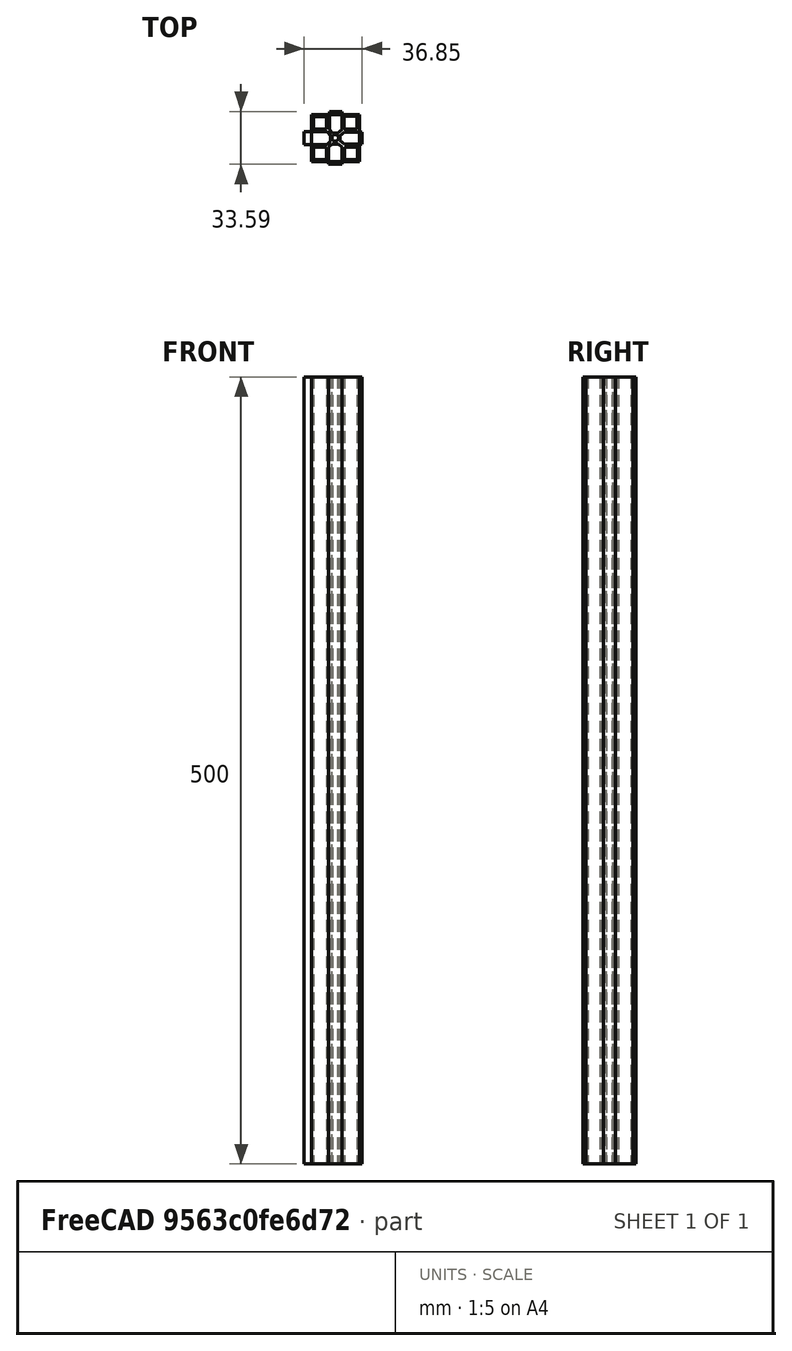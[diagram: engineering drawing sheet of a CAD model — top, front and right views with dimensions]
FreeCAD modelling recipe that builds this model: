
FCSTD DOCUMENT  (FreeCAD 0.16R6712 (Git))
Label: Perfil - Gslot
License: All rights reserved
LicenseURL: http://en.wikipedia.org/wiki/All_rights_reserved
objects: Sketcher::SketchObject×2, PartDesign::Pad×1, PartDesign::Pocket×1
note: 6 computed .brp shape members not serialized (recipe doc carries the construction recipe); baked Part::Feature solids carry a one-line shape summary decoded from their .brp

FEATURE [Sketcher::SketchObject] Sketch
  sketch-geometry (4):
    g0: LineSegment StartX=0 StartY=0 StartZ=0 EndX=30.196 EndY=0 EndZ=0
    g1: LineSegment StartX=30.196 StartY=0 StartZ=0 EndX=30.196 EndY=30.0184 EndZ=0
    g2: LineSegment StartX=30.196 StartY=30.0184 StartZ=0 EndX=0 EndY=30.0184 EndZ=0
    g3: LineSegment StartX=0 StartY=30.0184 StartZ=0 EndX=0 EndY=0 EndZ=0
  constraints (9):
    c: Coincident(g0,g1)
    c: Coincident(g1,g2)
    c: Coincident(g2,g3)
    c: Coincident(g3,g0)
    c: Horizontal(g0)
    c: Horizontal(g2)
    c: Vertical(g1)
    c: Vertical(g3)
    c: Coincident(g0,g-1)
FEATURE [PartDesign::Pad] Pad
  Length = 500
  Length2 = 100
  Sketch = -> Sketch
  Type = 0
FEATURE [Sketcher::SketchObject] Sketch001
  Placement = pos=(0,0,500) rot=(0,0,1;0rad)
  Support = -> Pad [Face6]
  sketch-geometry (41):
    g0: LineSegment StartX=1.26476 StartY=9.4367 StartZ=0 EndX=9.454 EndY=9.4367 EndZ=0
    g1: LineSegment StartX=9.454 StartY=9.4367 StartZ=0 EndX=9.454 EndY=1.24745 EndZ=0
    g2: LineSegment StartX=9.454 StartY=1.24745 StartZ=0 EndX=1.26476 EndY=1.24745 EndZ=0
    g3: LineSegment StartX=1.26476 StartY=1.24745 StartZ=0 EndX=1.26476 EndY=9.4367 EndZ=0
    g4: LineSegment StartX=20.8215 StartY=9.16912 StartZ=0 EndX=29.0249 EndY=9.16912 EndZ=0
    g5: LineSegment StartX=29.0249 StartY=9.16912 StartZ=0 EndX=29.0249 EndY=1.31685 EndZ=0
    g6: LineSegment StartX=29.0249 StartY=1.31685 StartZ=0 EndX=20.8215 EndY=1.31685 EndZ=0
    g7: LineSegment StartX=20.8215 StartY=1.31685 StartZ=0 EndX=20.8215 EndY=9.16912 EndZ=0
    g8: LineSegment StartX=20.4824 StartY=28.981 StartZ=0 EndX=28.8043 EndY=28.981 EndZ=0
    g9: LineSegment StartX=28.8043 StartY=28.981 StartZ=0 EndX=28.8043 EndY=20.8361 EndZ=0
    g10: LineSegment StartX=28.8043 StartY=20.8361 StartZ=0 EndX=20.4824 EndY=20.8361 EndZ=0
    g11: LineSegment StartX=20.4824 StartY=20.8361 StartZ=0 EndX=20.4824 EndY=28.981 EndZ=0
    g12: LineSegment StartX=1.10227 StartY=28.634 StartZ=0 EndX=9.44748 EndY=28.634 EndZ=0
    g13: LineSegment StartX=9.44748 StartY=28.634 StartZ=0 EndX=9.44748 EndY=20.6125 EndZ=0
    g14: LineSegment StartX=9.44748 StartY=20.6125 StartZ=0 EndX=1.10227 EndY=20.6125 EndZ=0
    g15: LineSegment StartX=1.10227 StartY=20.6125 StartZ=0 EndX=1.10227 EndY=28.634 EndZ=0
    g16: Circle CenterX=14.8879 CenterY=15.1875 CenterZ=0 NormalX=0 NormalY=0 NormalZ=1 Radius=2.12423
    g17: LineSegment StartX=19.1701 StartY=9.2285 StartZ=0 EndX=19.1701 EndY=-1.66736 EndZ=0
    g18: LineSegment StartX=19.1701 StartY=-1.66736 StartZ=0 EndX=10.7726 EndY=-1.66736 EndZ=0
    g19: LineSegment StartX=10.7726 StartY=-1.66736 StartZ=0 EndX=10.7726 EndY=9.2285 EndZ=0
    g20: LineSegment StartX=32.0785 StartY=11.3105 StartZ=0 EndX=20.8357 EndY=11.3105 EndZ=0
    g21: LineSegment StartX=20.8357 StartY=18.8752 StartZ=0 EndX=32.0785 EndY=18.8752 EndZ=0
    g22: LineSegment StartX=32.0785 StartY=18.8752 StartZ=0 EndX=32.0785 EndY=11.3105 EndZ=0
    g23: LineSegment StartX=11.189 StartY=31.9224 StartZ=0 EndX=19.2395 EndY=31.9224 EndZ=0
    g24: LineSegment StartX=19.2395 StartY=31.9224 StartZ=0 EndX=19.2395 EndY=20.402 EndZ=0
    g25: LineSegment StartX=11.189 StartY=20.402 StartZ=0 EndX=11.189 EndY=31.9224 EndZ=0
    g26: LineSegment StartX=-4.77307 StartY=19.1528 StartZ=0 EndX=9.6622 EndY=19.1528 EndZ=0
    g27: LineSegment StartX=9.6622 StartY=10.9635 StartZ=0 EndX=-4.77307 EndY=10.9635 EndZ=0
    g28: LineSegment StartX=-4.77307 StartY=10.9635 StartZ=0 EndX=-4.77307 EndY=19.1528 EndZ=0
    g29: LineSegment StartX=12.8546 StartY=11.1023 StartZ=0 EndX=17.088 EndY=11.1023 EndZ=0
    g30: LineSegment StartX=17.088 StartY=11.1023 StartZ=0 EndX=19.1701 EndY=9.2285 EndZ=0
    g31: LineSegment StartX=12.8546 StartY=11.1023 StartZ=0 EndX=10.7726 EndY=9.2285 EndZ=0
    g32: LineSegment StartX=13.2016 StartY=18.0423 StartZ=0 EndX=16.4634 EndY=18.0423 EndZ=0
    g33: LineSegment StartX=16.4634 StartY=18.0423 StartZ=0 EndX=19.2395 EndY=20.402 EndZ=0
    g34: LineSegment StartX=13.2016 StartY=18.0423 StartZ=0 EndX=11.189 EndY=20.402 EndZ=0
    g35: LineSegment StartX=17.9902 StartY=16.5849 StartZ=0 EndX=17.9902 EndY=13.2537 EndZ=0
    g36: LineSegment StartX=17.9902 StartY=13.2537 StartZ=0 EndX=20.8357 EndY=11.3105 EndZ=0
    g37: LineSegment StartX=17.9902 StartY=16.5849 StartZ=0 EndX=20.8357 EndY=18.8752 EndZ=0
    g38: LineSegment StartX=11.8136 StartY=16.6543 StartZ=0 EndX=11.8136 EndY=13.0455 EndZ=0
    g39: LineSegment StartX=11.8136 StartY=13.0455 StartZ=0 EndX=9.6622 EndY=10.9635 EndZ=0
    g40: LineSegment StartX=11.8136 StartY=16.6543 StartZ=0 EndX=9.6622 EndY=19.1528 EndZ=0
  constraints (67):
    c: Coincident(g0,g1)
    c: Coincident(g1,g2)
    c: Coincident(g2,g3)
    c: Coincident(g3,g0)
    c: Horizontal(g0)
    c: Horizontal(g2)
    c: Vertical(g1)
    c: Vertical(g3)
    c: Coincident(g4,g5)
    c: Coincident(g5,g6)
    c: Coincident(g6,g7)
    c: Coincident(g7,g4)
    c: Horizontal(g4)
    c: Horizontal(g6)
    c: Vertical(g5)
    c: Vertical(g7)
    c: Coincident(g8,g9)
    c: Coincident(g9,g10)
    c: Coincident(g10,g11)
    c: Coincident(g11,g8)
    c: Horizontal(g8)
    c: Horizontal(g10)
    c: Vertical(g9)
    c: Vertical(g11)
    c: Coincident(g12,g13)
    c: Coincident(g13,g14)
    c: Coincident(g14,g15)
    c: Coincident(g15,g12)
    c: Horizontal(g12)
    c: Horizontal(g14)
    c: Vertical(g13)
    c: Vertical(g15)
    c: Coincident(g17,g18)
    c: Coincident(g18,g19)
    c: Horizontal(g18)
    c: Vertical(g17)
    c: Vertical(g19)
    c: Coincident(g21,g22)
    c: Coincident(g22,g20)
    c: Horizontal(g20)
    c: Horizontal(g21)
    c: Vertical(g22)
    c: Coincident(g23,g24)
    c: Coincident(g25,g23)
    c: Horizontal(g23)
    c: Vertical(g24)
    c: Vertical(g25)
    c: Coincident(g27,g28)
    c: Coincident(g28,g26)
    c: Horizontal(g26)
    c: Horizontal(g27)
    c: Vertical(g28)
    c: Horizontal(g29)
    c: Coincident(g30,g29)
    c: Coincident(g31,g29)
    c: Horizontal(g32)
    c: Coincident(g33,g32)
    c: Coincident(g33,g24)
    c: Coincident(g34,g32)
    c: Vertical(g35)
    c: Coincident(g36,g35)
    c: Coincident(g36,g20)
    c: Coincident(g37,g35)
    c: Vertical(g38)
    c: Coincident(g39,g38)
    c: Coincident(g40,g38)
    c: Coincident(g40,g26)
FEATURE [PartDesign::Pocket] Pocket
  Length = 500
  Sketch = -> Sketch001
  Type = 0
